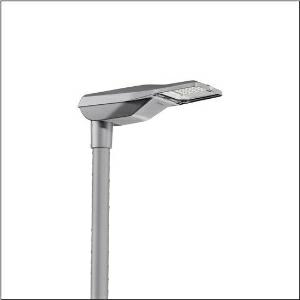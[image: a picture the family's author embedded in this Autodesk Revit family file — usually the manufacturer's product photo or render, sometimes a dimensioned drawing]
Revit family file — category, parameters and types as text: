
# Revit family: streetlight_sl_21_iq_micro___st0_8a_5xe1c41g08db_305a
name_source: partatom
category: Lighting Fixtures
units: mm (PartAtom-declared; Revit-internal decimal feet)

## family parameters
Cut with Voids When Loaded = No
Host = Face
Light Source = No
Part Type = Normal
Room Calculation Point = No
Round Connector Dimension = Use Diameter
Shared = No

## types (1)
- --- (1 x LED, 5010 lm, 36.4 W, 4000K)
    Apparent Load = 36 VA
    CIE Flux Codes = 38 75 97 100 100
    Color Rendering = 70
    Color Temperature = 4000K
    Default Elevation = 1800 mm
    Description = Streetlight SL 21 iQ micro, mast luminaire, primary light control with lens, of PMMA, primary optical cover: cover, of toughened safety glass, transparent, light distribution: ST0.8a, light emission: direct distribution, primary light characteristic: asymmetric, installation type: post-top, side-entry, LED, High Power LED, rated luminous flux: 5.010lm, luminous efficacy: 138lm/W, light colour: 740, colour temperature: 4000K, control gear: iQ Street-Remote, control: Street-Remote, Auto-Match, Temp-Guard, Lumen-Switch, Night-Set, Smart-Wire, Light-Fading, Desk-Remote (wireless, voltage-free reading and setting of iQ features in the workshop via application-optimized NFC function/RFID function), optimised constant luminous flux control (CLO 2.0), pre-setting: linear dimming characteristic, mains connection: 220..240V, AC, 50/60Hz, start of lifetime: 36W, end of service life: 38W, reduction: 16W, luminaire housing, of diecast aluminium, powder-coated, Siteco® metallic grey (DB 702S), corrosivity category C5 mid according to DIN EN ISO 12944, please order mast flange separately, inclination adjustable: 0°, 5°, 10°, 15°, sealing non-destructively replaceable, multi-level sealing system, length: 528mm, width: 235mm, height: 110mm, mast flange for spigot size: 42mm (side-entry): 5XC10008XM4, 60/48mm (side-entry/post-top): 5XC10108XM2, 76/60mm (side-entry/post-top): 5XC10108XM1, protection rating (complete): IP66, insulation class (complete): insulation class II (safety insulation), certification: CE, ENEC, ENEC+, VDE, impact resistance: IK10, permissible operating ambient temperature for outdoor applications: -40..+50°C, standard-compliant lighting for roads and squares, packaging unit: 1 piece

Light Distribution: ST0.8a
    Height = 110 mm
    Lamp = 1 x LED
    Lamp Light Flux = 5010 lm
    Lamp Power = 36.4 W
    Lamp count = 1
    Length = 528 mm
    Luminous efficacy = 138 lm/W
    Manufacturer = Siteco
    ModVariant = No
    Model = 5XE1C41G08DB
    Number of Poles = 1
    OnlyDefault = Yes
    Power Factor = 1
    Product Name = Streetlight SL 21 iQ micro | ST0.8a
    Product group = mast luminaire | pylon top
    ProductGroupID = 6100
    Protection Class = Protection class II
    Protection Degree = IP 66
    RLX_Detail_Level = 1
    RLX_Emergency_Light_Flux = 0 lm
    RLX_Emergency_Type = 0
    RLX_Emergency_Type_DB = No
    RlxData = <blob elided: 98881 chars, md5=f89c4a2f>
    Socket = socket
    Standby Power = 0 W
    System Light Flux = 5010 lm
    System Power = 36 W
    Type Comments = factory setting: luminous flux: 100 % | dim-lin: 254 | 715 mA
    Type Image = l_1006881.jpg
    URL = http://relux.com
    VarID = @adj_175945
    Voltage = 0 V
    Weight = 0.00 kg
    Width = 235 mm

## geometry (parser evidence)
native form markers: Blend x4, Sweep x10
no freeform markers — native parametric forms only
